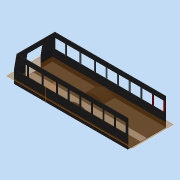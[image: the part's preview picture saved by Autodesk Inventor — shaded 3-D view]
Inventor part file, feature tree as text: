
AUTODESK INVENTOR PART (.ipt)
format: ipt  version: 2018.2 (Build 222227000, 227)  size: 550,400 bytes
history: native  units: in
note: dims shown in document units (in); Inventor stores cm internally (conversion verified against a paired STEP export)
features: extrude x47, sketch x14, plane x2, projected_geometry x2
ambient origin geometry x8: Origin, YZ Plane, XZ Plane, XY Plane, X Axis, Y Axis, Z Axis, Center Point
bodies: Solid1 (feature_tree)
feature tree (65):
  extrude  "Extrusion1"  Depth=92.5in
  extrude  "Extrusion2"  Depth=1.0in
  sketch  "Sketch3"  dims[d5=64.75in d6=0.0in d7=28.25in]
  extrude  "Extrusion3"  Depth=28.25in
  extrude  "Extrusion4"  Depth=64.75in TaperAngle=0.0deg
  sketch  "Sketch5"  dims[d9=1.0in d10=64.75in d11=0.0in]
  extrude  "Extrusion6"  Depth=6.5in
  extrude  "Extrusion7"  Depth=24.5in
  extrude  "Extrusion8"  Depth=3.5in
  extrude  "Extrusion9"  Depth=3.5in
  extrude  "Extrusion10"  Depth=3.5in
  extrude  "Extrusion11"  Depth=3.5in
  extrude  "Extrusion12"  Depth=3.5in
  extrude  "Extrusion13"  Depth=3.5in
  extrude  "Extrusion14"  Depth=3.5in
  sketch  "Sketch6"  dims[d12=64.75in d13=0.0in d16=6.5in]
  extrude  "Extrusion15"  Depth=3.75in
  extrude  "Extrusion16"  Depth=24.0in
  extrude  "Extrusion17"  Depth=3.75in
  extrude  "Extrusion18"  Depth=1.0in TaperAngle=0.0deg
  extrude  "Extrusion19"  Depth=1.0in TaperAngle=0.0deg
  extrude  "Extrusion20"  Depth=1.0in TaperAngle=0.0deg
  extrude  "Extrusion21"  Depth=1.0in TaperAngle=0.0deg
  extrude  "Extrusion22"  Depth=1.0in TaperAngle=0.0deg
  extrude  "Extrusion23"  Depth=1.0in TaperAngle=0.0deg
  sketch  "Sketch7"  dims[d17=29.5in d18=24.5in]
  extrude  "Extrusion24"  Depth=1.0in TaperAngle=0.0deg
  extrude  "Extrusion25"  Depth=1.0in TaperAngle=0.0deg
  extrude  "Extrusion26"  Depth=1.0in TaperAngle=0.0deg
  extrude  "Extrusion27"  Depth=3.75in
  extrude  "Extrusion28"  Depth=0.25in TaperAngle=0.0deg
  extrude  "Extrusion29"  Depth=0.25in TaperAngle=0.0deg
  extrude  "Extrusion30"  Depth=0.25in TaperAngle=0.0deg
  extrude  "Extrusion31"  Depth=0.25in TaperAngle=0.0deg
  extrude  "Extrusion32"  Depth=0.25in TaperAngle=0.0deg
  sketch  "Sketch8"  dims[d19=23.75in d20=3.5in]
  extrude  "Extrusion33"  Depth=0.25in TaperAngle=0.0deg
  extrude  "Extrusion34"  Depth=0.25in TaperAngle=0.0deg
  extrude  "Extrusion35"  Depth=0.25in TaperAngle=0.0deg
  extrude  "Extrusion36"  Depth=0.25in TaperAngle=0.0deg
  extrude  "Extrusion37"  Depth=1.0in TaperAngle=0.0deg
  extrude  "Extrusion38"  Depth=1.0in TaperAngle=0.0deg
  extrude  "Extrusion39"  Depth=1.0in TaperAngle=0.0deg
  extrude  "Extrusion40"  Depth=1.0in TaperAngle=0.0deg
  extrude  "Extrusion41"  Depth=1.0in TaperAngle=0.0deg
  extrude  "Extrusion42"  Depth=1.0in TaperAngle=0.0deg
  extrude  "Extrusion43"  Depth=1.0in TaperAngle=0.0deg
  extrude  "Extrusion44"  Depth=1.0in TaperAngle=0.0deg
  extrude  "Extrusion45"  Depth=1.0in TaperAngle=0.0deg
  plane  "Work Plane1"
  extrude  "Extrusion46"  Depth=0.25in TaperAngle=0.0deg
  plane  "Work Plane2"
  extrude  "Extrusion47"  Depth=3.5in
  extrude  "Extrusion48"  Depth=0.25in TaperAngle=0.0deg
  sketch  "Sketch1"  dims[d0=275.0in d1=92.5in]
  sketch  "Sketch2"  dims[d2=1.0in d3=0.0in d4=1.0in]
  projected_geometry  "Projected Loop1"
  projected_geometry  "Projected Loop3"
  sketch  "Sketch9"  dims[d21=31.5in d22=3.5in]
  sketch  "Sketch10"  dims[d24=31.5in d25=3.5in]
  sketch  "Sketch11"  dims[d26=24.5in d27=3.5in]
  sketch  "Sketch12"  dims[d28=24.5in d29=3.5in]
  sketch  "Sketch13"  dims[d30=24.5in d31=3.5in]
  sketch  "Sketch14"  dims[d32=24.5in d33=3.5in]
  sketch  "Sketch15"  dims[d35=24.5in d36=3.75in d37=24.0in d38=3.75in d39=1.0in d40=0.0in d41=1.0in d42=0.0in d43=1.0in d44=0.0in d45=1.0in d46=0.0in d47=1.0in d48=0.0in d49=1.0in d50=0.0in d51=1.0in d52=0.0in d53=1.0in d54=0.0in d55=1.0in d56=0.0in d57=3.75in d58=0.25in d59=0.0in d60=0.25in d61=0.0in d62=0.25in d63=0.0in d64=0.25in d65=0.0in d66=0.25in d67=0.0in d68=0.25in d69=0.0in d70=0.25in d71=0.0in d72=0.25in d73=0.0in d74=0.25in d75=0.0in d79=1.0in d80=0.0in d81=1.0in d82=0.0in d83=1.0in d84=0.0in d85=1.0in d86=0.0in d87=1.0in d88=0.0in d89=1.0in d90=0.0in d91=1.0in d92=0.0in d93=1.0in d94=0.0in d95=1.0in d96=0.0in d98=0.25in d99=0.0in d100=3.5in d101=0.25in d102=0.0in d103=0.25in d104=0.0in d105=0.25in d106=0.0in d107=0.25in d108=0.0in d109=0.25in d110=0.0in d111=0.25in d112=0.0in d113=0.25in d114=0.0in d115=0.25in d116=0.0in d117=104.5in d118=180.0deg d119=46.5in d121=26.0in d122=0.0in d123=104.5in d124=46.5in d126=26.0in d127=0.0in d128=30.25in d129=14.75in d130=0.001in d131=0.001in d132=0.0in d133=26.625in d134=50.75in d135=90.0deg d136=37.25in d137=13.3135in d138=0.0in d139=75.75in d142=8.375in d143=0.0in d144=10.375in d145=1.125in d146=0.25in d147=0.0in d148=1.125in d149=0.25in d150=0.0in]
